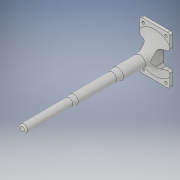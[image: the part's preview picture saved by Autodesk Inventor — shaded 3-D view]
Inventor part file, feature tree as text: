
AUTODESK INVENTOR PART (.ipt)
format: ipt  version: 2019 (Build 230136000, 136)  size: 245,248 bytes
history: native  units: mm
features: sketch x5, extrude x4, fillet x4, hole x1
ambient origin geometry x8: Origin, YZ Plane, XZ Plane, XY Plane, X Axis, Y Axis, Z Axis, Center Point
bodies: Body1 (feature_tree)
feature tree (14):
  sketch  "Sketch1"  dims[d0=41.0mm d1=65.3mm d2=21.0mm d3=21.0mm d4=12.0mm d9=5.0mm d11=5.0mm d12=41.0mm d13=41.0mm d14=12.0mm d19=5.0mm d20=5.0mm]
  extrude  "Extrusion3"  Depth=5.0mm
  hole  "Hole2"  [1 undecoded]
  fillet  "Fillet2"  Radius=15.0mm
  extrude  "Extrusion4"  Depth=8.5mm
  extrude  "Extrusion5"  Depth=20.0mm
  extrude  "Extrusion6"  Depth=20.0mm
  fillet  "Fillet5"  Radius=60.0mm
  fillet  "Fillet6"  Radius=10.0mm
  fillet  "Fillet7"  Radius=70.0mm
  sketch  "Sketch5"  dims[d53=41.0mm d54=65.3mm d55=21.0mm d56=21.0mm d57=12.0mm d58=5.0mm d59=5.0mm d60=41.0mm d61=41.0mm d62=12.0mm d63=10.5mm d64=10.5mm d65=5.0mm d66=5.0mm d67=4.0mm d68=0.0mm]
  sketch  "Sketch6"  dims[d69=3.6mm d70=6.0mm d71=4.0mm d72=2.0mm d73=90.0deg d74=8.0mm d75=20.594885mm d76=15.0mm]
  sketch  "Sketch7"  dims[d77=50.0mm d78=0.0mm d79=8.5mm]
  sketch  "Sketch8"  dims[d80=32.65mm d81=3.0mm d83=12.0mm d84=60.0mm d85=0.0mm d86=10.0mm d87=70.0mm d88=0.0mm d90=2.0mm d91=20.0mm d92=20.0mm]
note: 1 required parameter value undecoded (feature->parameter linkage not recoverable at this tier; creation-order binding heuristic only, values carry confidence <= 0.55)
